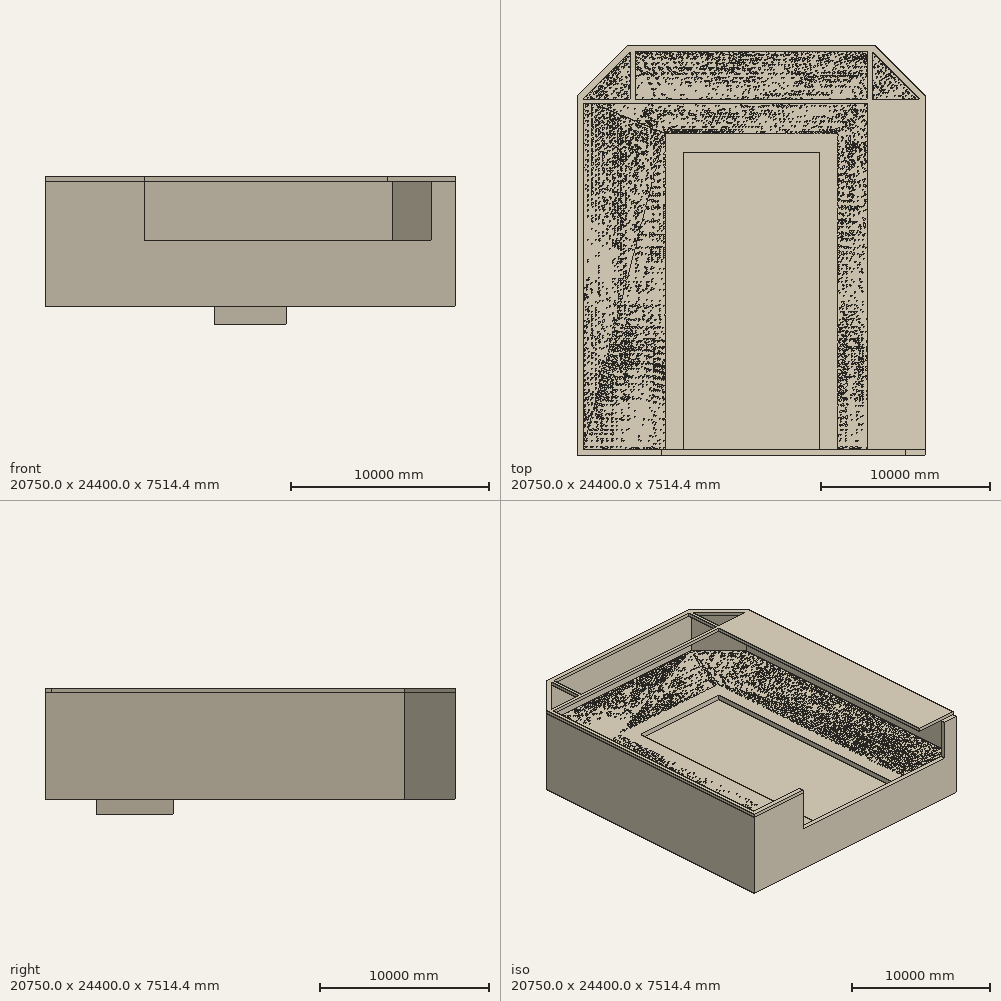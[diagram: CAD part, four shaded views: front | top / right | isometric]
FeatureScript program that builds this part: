
annotation { "Feature Type Name" : "Feature", "Feature Type Description" : "" }
export const myFeature = defineFeature(function(context is Context, id is Id, definition is map)
    precondition{}
    {
        {
            var Q0;
            Q0=qCreatedBy(makeId("Top.planeOp"),FACE);
            var sketch = newSketch(context, id + "F0", { "sketchPlane" : qUnion([Q0])});
            skLineSegment(sketch, "E0.bottom", {"start": v(-7325, 12200) * mm, "end": v(7325, 12200) * mm});
            skLineSegment(sketch, "E0.top", {"start": v(-10375, -12200) * mm, "end": v(10375, -12200) * mm});
            skLineSegment(sketch, "E0.left", {"start": v(-10375, 9150) * mm, "end": v(-10375, -12200) * mm});
            skLineSegment(sketch, "E0.right", {"start": v(10375, 9150) * mm, "end": v(10375, -12200) * mm});
            skLineSegment(sketch, "E1", {"start": v(0, 0) * mm, "end": v(0, -12200) * mm, "construction": true});
            skLineSegment(sketch, "E2", {"start": v(-10375, 0) * mm, "end": v(0, 0) * mm, "construction": true});
            skLineSegment(sketch, "E3", {"start": v(7325, 12200) * mm, "end": v(10375, 9150) * mm});
            skLineSegment(sketch, "E4", {"start": v(-7325, 12200) * mm, "end": v(-10375, 9150) * mm});
            skSolve(sketch);
        }
        {
            var Q0;
            Q0=makeQuery(id+"F0.imprint","IMPRINT",FACE,{"disambiguationData":[TD([[makeQuery(id+"F0.imprint","IMPRINT",EDGE,{"derivedFrom":sQuery(id+"F0.wireOp",EDGE,"E0.bottom")}),-1.0]])]});
            extrude(context, id + "F1", {"entities" : qUnion([Q0]), "offsetDistance" : 25 * mm, "depth" : 6350 * mm});
        }
        {
            var Q0;
            Q0=makeQuery(id+"F1.opExtrude","CAP_FACE",FACE,{"disambiguationData":[OSD([sQuery(id+"F0.wireOp",EDGE,"E0.bottom"),sQuery(id+"F0.wireOp",EDGE,"E0.top"),sQuery(id+"F0.wireOp",EDGE,"E0.left"),sQuery(id+"F0.wireOp",EDGE,"E0.right"),sQuery(id+"F0.wireOp",EDGE,"E3"),sQuery(id+"F0.wireOp",EDGE,"E4")])],"isStart":false});
            shell(context, id + "F2", {"entities" : qUnion([Q0]), "thickness" : 350 * mm});
        }
        {
            var Q0;
            Q0=makeQuery(id+"F1.opExtrude","SWEPT_FACE",FACE,{"disambiguationData":[OSD([sQuery(id+"F0.wireOp",EDGE,"E0.top")])]});
            var sketch = newSketch(context, id + "F3", { "sketchPlane" : qUnion([Q0])});
            skLineSegment(sketch, "E5.bottom", {"start": v(-5375, 6350) * mm, "end": v(9155, 6350) * mm});
            skLineSegment(sketch, "E5.top", {"start": v(-5375, 3350) * mm, "end": v(9155, 3350) * mm});
            skLineSegment(sketch, "E5.left", {"start": v(-5375, 6350) * mm, "end": v(-5375, 3350) * mm});
            skLineSegment(sketch, "E5.right", {"start": v(9155, 6350) * mm, "end": v(9155, 3350) * mm});
            skLineSegment(sketch, "E6.bottom", {"start": v(-4375, 3350) * mm, "end": v(8375, 3350) * mm});
            skLineSegment(sketch, "E6.top", {"start": v(-4375, 310) * mm, "end": v(8375, 310) * mm});
            skLineSegment(sketch, "E6.left", {"start": v(-4375, 3350) * mm, "end": v(-4375, 310) * mm});
            skLineSegment(sketch, "E6.right", {"start": v(8375, 3350) * mm, "end": v(8375, 310) * mm});
            skLineSegment(sketch, "E7.0", {"start": v(-10380, -5) * mm, "end": v(10380, -5) * mm});
            skLineSegment(sketch, "E7.1", {"start": v(-10380, 6355) * mm, "end": v(-10380, -5) * mm});
            skLineSegment(sketch, "E7.2", {"start": v(10380, 6355) * mm, "end": v(-10380, 6355) * mm});
            skLineSegment(sketch, "E7.3", {"start": v(10380, -5) * mm, "end": v(10380, 6355) * mm});
            skSolve(sketch);
        }
        {
            var Q0;
            Q0=makeQuery(id+"F3.imprint","IMPRINT",FACE,{"disambiguationData":[TD([[makeQuery(id+"F3.imprint","IMPRINT",EDGE,{"derivedFrom":sQuery(id+"F3.wireOp",EDGE,"E6.bottom")}),-1.0]])]});
            var Q1;
            Q1=makeQuery(id+"F3.imprint","IMPRINT",FACE,{"disambiguationData":[TD([[makeQuery(id+"F3.imprint","IMPRINT",EDGE,{"derivedFrom":sQuery(id+"F3.wireOp",EDGE,"E5.bottom")}),-1.0]])]});
            var Q2;
            Q2=makeQuery(id+"F2.opShell","OFFSET_FACE",FACE,{"disambiguationData":[OSD([sQuery(id+"F0.wireOp",EDGE,"E0.top")])]});
            extrude(context, id + "F4", {"entities" : qUnion([Q0, Q1]), "operationType" : NewBodyOperationType.REMOVE, "endBound" : BoundingType.UP_TO_SURFACE, "oppositeDirection" : true, "endBoundEntityFace" : qUnion([Q2]), "depth" : 300 * mm, "offsetDistance" : 25 * mm});
        }
        {
            var Q0;
            Q0=makeQuery(id+"F1.opExtrude","CAP_FACE",FACE,{"disambiguationData":[OSD([sQuery(id+"F0.wireOp",EDGE,"E0.bottom"),sQuery(id+"F0.wireOp",EDGE,"E0.top"),sQuery(id+"F0.wireOp",EDGE,"E0.left"),sQuery(id+"F0.wireOp",EDGE,"E0.right"),sQuery(id+"F0.wireOp",EDGE,"E3"),sQuery(id+"F0.wireOp",EDGE,"E4")])],"isStart":false});
            var sketch = newSketch(context, id + "F5", { "sketchPlane" : qUnion([Q0])});
            skLineSegment(sketch, "E8.0", {"start": v(-10375, 9150) * mm, "end": v(-10375, -12200) * mm});
            skLineSegment(sketch, "E8.1", {"start": v(-7325, 12200) * mm, "end": v(-10375, 9150) * mm});
            skLineSegment(sketch, "E8.2", {"start": v(-7325, 12200) * mm, "end": v(7325, 12200) * mm});
            skLineSegment(sketch, "E8.3", {"start": v(7325, 12200) * mm, "end": v(10375, 9150) * mm});
            skLineSegment(sketch, "E8.4", {"start": v(10375, 9150) * mm, "end": v(10375, -12200) * mm});
            skLineSegment(sketch, "E8.5", {"start": v(-10375, -12200) * mm, "end": v(-5375, -12200) * mm});
            skLineSegment(sketch, "E8.6", {"start": v(-10025, 9005.03) * mm, "end": v(-10025, -11850) * mm});
            skLineSegment(sketch, "E8.7", {"start": v(-7180.03, 11850) * mm, "end": v(-10025, 9005.03) * mm});
            skLineSegment(sketch, "E8.8", {"start": v(-7180.03, 11850) * mm, "end": v(7180.03, 11850) * mm});
            skLineSegment(sketch, "E8.9", {"start": v(7180.03, 11850) * mm, "end": v(10025, 9005.03) * mm});
            skLineSegment(sketch, "E8.10", {"start": v(10025, 9005.03) * mm, "end": v(10025, -11850) * mm});
            skLineSegment(sketch, "E8.11", {"start": v(-10025, -11850) * mm, "end": v(-5000, -11850) * mm});
            skLineSegment(sketch, "E9.bottom", {"start": v(-5000, -11850) * mm, "end": v(10375, -11850) * mm});
            skLineSegment(sketch, "E9.top", {"start": v(-5000, -12200) * mm, "end": v(10375, -12200) * mm});
            skLineSegment(sketch, "E9.right", {"start": v(10375, -11850) * mm, "end": v(10375, -12200) * mm});
            skLineSegment(sketch, "E10", {"start": v(-10025, 9005.03) * mm, "end": v(-7180.03, 9005.03) * mm});
            skLineSegment(sketch, "E11", {"start": v(-7180.03, 9005.03) * mm, "end": v(-7180.03, 11850) * mm});
            skLineSegment(sketch, "E12", {"start": v(7180.03, 11850) * mm, "end": v(7180.03, 9005.03) * mm});
            skLineSegment(sketch, "E13", {"start": v(7180.03, 9005.03) * mm, "end": v(10025, 9005.03) * mm});
            skLineSegment(sketch, "E14", {"start": v(-7180.03, 9005.03) * mm, "end": v(7180.03, 9005.03) * mm});
            skLineSegment(sketch, "E15", {"start": v(-7180.03, 9005.03) * mm, "end": v(-7180.03, -7244.51) * mm});
            skLineSegment(sketch, "E16", {"start": v(7180.03, 9005.03) * mm, "end": v(7180.03, -11850) * mm});
            skLineSegment(sketch, "E17", {"start": v(-10025, 8751.03) * mm, "end": v(10025, 8751.03) * mm});
            skLineSegment(sketch, "E18", {"start": v(-6926.03, 11850) * mm, "end": v(-6926.03, -11850) * mm});
            skLineSegment(sketch, "E19", {"start": v(6926.03, 11850) * mm, "end": v(6926.03, -11850) * mm});
            skSolve(sketch);
        }
        {
            var Q0;
            Q0=makeQuery(id+"F5.imprint","IMPRINT",FACE,{"disambiguationData":[TD([[makeQuery(id+"F5.imprint","IMPRINT",EDGE,{"derivedFrom":sQuery(id+"F5.wireOp",EDGE,"E8.0")}),1.0]])]});
            var Q1;
            {var subQ0=sQuery(id+"F5.wireOp",EDGE,"E9.left");Q1=makeQuery(id+"F5.imprint","IMPRINT",FACE,{"disambiguationData":[TD([[makeQuery(id+"F5.imprint","IMPRINT",EDGE,{"derivedFrom":subQ0}),1.0]])]});}
            var Q2;
            {var subQ0=sQuery(id+"F5.wireOp",EDGE,"E9.right");Q2=makeQuery(id+"F5.imprint","IMPRINT",FACE,{"disambiguationData":[TD([[makeQuery(id+"F5.imprint","IMPRINT",EDGE,{"derivedFrom":subQ0}),-1.0]])]});}
            var Q3;
            {var subQ0=sQuery(id+"F5.wireOp",EDGE,"E10");Q3=makeQuery(id+"F5.imprint","IMPRINT",FACE,{"disambiguationData":[TD([[makeQuery(id+"F5.imprint","IMPRINT",EDGE,{"derivedFrom":subQ0}),-1.0]])]});}
            var Q4;
            {var subQ0=sQuery(id+"F5.wireOp",EDGE,"E15");var subQ5=sQuery(id+"F5.wireOp",EDGE,"E17");var subQ6=makeQuery(id+"F5.imprint","INTERSECT",VERTEX,{"derivedFrom":[subQ0,subQ5]});Q4=makeQuery(id+"F5.imprint","IMPRINT",FACE,{"disambiguationData":[TD([[makeQuery(id+"F5.imprint","IMPRINT",EDGE,{"disambiguationData":[TD([[subQ6,-1.0]])],"derivedFrom":subQ5}),1.0]])]});}
            var Q5;
            {var subQ0=sQuery(id+"F5.wireOp",EDGE,"E11");Q5=makeQuery(id+"F5.imprint","IMPRINT",FACE,{"disambiguationData":[TD([[makeQuery(id+"F5.imprint","IMPRINT",EDGE,{"derivedFrom":subQ0}),-1.0]])]});}
            var Q6;
            {var subQ0=sQuery(id+"F5.wireOp",EDGE,"E18");var subQ1=sQuery(id+"F5.wireOp",EDGE,"E14");var subQ2=makeQuery(id+"F5.imprint","INTERSECT",VERTEX,{"derivedFrom":[subQ1,subQ0]});Q6=makeQuery(id+"F5.imprint","IMPRINT",FACE,{"disambiguationData":[TD([[makeQuery(id+"F5.imprint","IMPRINT",EDGE,{"disambiguationData":[TD([[subQ2,-1.0]])],"derivedFrom":subQ1}),-1.0]])]});}
            var Q7;
            {var subQ0=sQuery(id+"F5.wireOp",EDGE,"E12");Q7=makeQuery(id+"F5.imprint","IMPRINT",FACE,{"disambiguationData":[TD([[makeQuery(id+"F5.imprint","IMPRINT",EDGE,{"derivedFrom":subQ0}),-1.0]])]});}
            var Q8;
            {var subQ0=sQuery(id+"F5.wireOp",EDGE,"E16");var subQ5=sQuery(id+"F5.wireOp",EDGE,"E17");var subQ6=makeQuery(id+"F5.imprint","INTERSECT",VERTEX,{"derivedFrom":[subQ0,subQ5]});Q8=makeQuery(id+"F5.imprint","IMPRINT",FACE,{"disambiguationData":[TD([[makeQuery(id+"F5.imprint","IMPRINT",EDGE,{"disambiguationData":[TD([[subQ6,1.0]])],"derivedFrom":subQ5}),1.0]])]});}
            var Q9;
            {var subQ0=sQuery(id+"F5.wireOp",EDGE,"E13");Q9=makeQuery(id+"F5.imprint","IMPRINT",FACE,{"disambiguationData":[TD([[makeQuery(id+"F5.imprint","IMPRINT",EDGE,{"derivedFrom":subQ0}),-1.0]])]});}
            var Q10;
            {var subQ0=sQuery(id+"F5.wireOp",EDGE,"E16");var subQ1=sQuery(id+"F5.wireOp",EDGE,"E9.bottom");var subQ2=makeQuery(id+"F5.imprint","INTERSECT",VERTEX,{"derivedFrom":[subQ1,subQ0]});Q10=makeQuery(id+"F5.imprint","IMPRINT",FACE,{"disambiguationData":[TD([[makeQuery(id+"F5.imprint","IMPRINT",EDGE,{"disambiguationData":[TD([[subQ2,1.0]])],"derivedFrom":subQ1}),1.0]])]});}
            var Q11;
            {var subQ0=sQuery(id+"F5.wireOp",EDGE,"E18");var subQ1=sQuery(id+"F5.wireOp",EDGE,"E9.bottom");var subQ2=makeQuery(id+"F5.imprint","INTERSECT",VERTEX,{"derivedFrom":[subQ1,subQ0]});Q11=makeQuery(id+"F5.imprint","IMPRINT",FACE,{"disambiguationData":[TD([[makeQuery(id+"F5.imprint","IMPRINT",EDGE,{"disambiguationData":[TD([[subQ2,1.0]])],"derivedFrom":subQ1}),1.0]])]});}
            var Q12;
            {var subQ3=sQuery(id+"F3.wireOp",EDGE,"E5.bottom");var subQ4=sQuery(id+"F0.wireOp",EDGE,"E0.top");var subQ5=makeQuery(id+"F4.boolean.opBoolean","COPY",EDGE,{"derivedFrom":makeQuery(id+"F4.opExtrude","SWEPT_EDGE",EDGE,{"disambiguationData":[OSD([subQ4,subQ3,sQuery(id+"F3.wireOp",EDGE,"E5.left")])]})});Q12=makeQuery(id+"F5.imprint","IMPRINT",FACE,{"disambiguationData":[TD([[makeQuery(id+"F5.imprint","IMPRINT",EDGE,{"derivedFrom":subQ5}),1.0]])]});}
            extrude(context, id + "F6", {"entities" : qUnion([Q0, Q1, Q2, Q3, Q4, Q5, Q6, Q7, Q8, Q9, Q10, Q11, Q12]), "depth" : 250 * mm});
        }
        {
            var Q0;
            Q0=makeQuery(id+"F1.opExtrude","CAP_FACE",FACE,{"disambiguationData":[OSD([sQuery(id+"F0.wireOp",EDGE,"E0.bottom"),sQuery(id+"F0.wireOp",EDGE,"E0.top"),sQuery(id+"F0.wireOp",EDGE,"E0.left"),sQuery(id+"F0.wireOp",EDGE,"E0.right"),sQuery(id+"F0.wireOp",EDGE,"E3"),sQuery(id+"F0.wireOp",EDGE,"E4")])],"isStart":true});
            var sketch = newSketch(context, id + "F7", { "sketchPlane" : qUnion([Q0])});
            skLineSegment(sketch, "E20.bottom", {"start": v(-1828.8, 9152) * mm, "end": v(1828.8, 9152) * mm});
            skLineSegment(sketch, "E20.top", {"start": v(-1828.8, 4580) * mm, "end": v(1828.8, 4580) * mm});
            skLineSegment(sketch, "E20.left", {"start": v(-1828.8, 9152) * mm, "end": v(-1828.8, 4580) * mm});
            skLineSegment(sketch, "E20.right", {"start": v(1828.8, 9152) * mm, "end": v(1828.8, 4580) * mm});
            skLineSegment(sketch, "E21", {"start": v(0, 9152) * mm, "end": v(0, 12200) * mm, "construction": true});
            skSolve(sketch);
        }
        {
            var Q0;
            Q0=makeQuery(id+"F7.imprint","IMPRINT",FACE,{"disambiguationData":[TD([[makeQuery(id+"F7.imprint","IMPRINT",EDGE,{"derivedFrom":sQuery(id+"F7.wireOp",EDGE,"E20.bottom")}),-1.0]])]});
            extrude(context, id + "F8", {"entities" : qUnion([Q0]), "operationType" : NewBodyOperationType.ADD, "depth" : 914.4 * mm, "offsetDistance" : 25 * mm});
        }
        {
            var Q0;
            {var subQ0=sQuery(id+"F3.wireOp",EDGE,"E5.top");Q0=makeQuery(id+"F4.boolean.opBoolean","COPY",FACE,{"derivedFrom":makeQuery(id+"F4.opExtrude","SWEPT_FACE",FACE,{"disambiguationData":[OSD([subQ0]),TDD([makeQuery(id+"F3.imprint","IMPRINT",EDGE,{"disambiguationData":[TD([[makeQuery(id+"F3.imprint","INTERSECT",VERTEX,{"derivedFrom":[subQ0,sQuery(id+"F3.wireOp",EDGE,"E5.left")]}),-1.0]])],"derivedFrom":subQ0})])]})});}
            var sketch = newSketch(context, id + "F9", { "sketchPlane" : qUnion([Q0])});
            skLineSegment(sketch, "E22", {"start": v(-10025, -11850) * mm, "end": v(-10025, 9005.03) * mm});
            skLineSegment(sketch, "E23", {"start": v(-10025, 9005.03) * mm, "end": v(-7180.03, 11850) * mm});
            skLineSegment(sketch, "E24", {"start": v(-7180.03, 11850) * mm, "end": v(7180.03, 11850) * mm});
            skLineSegment(sketch, "E25", {"start": v(7180.03, 11850) * mm, "end": v(10025, 9005.03) * mm});
            skLineSegment(sketch, "E26", {"start": v(10025, 9005.03) * mm, "end": v(10025, -11850) * mm});
            skLineSegment(sketch, "E27", {"start": v(10025, -11850) * mm, "end": v(5148.2, -11850) * mm});
            skLineSegment(sketch, "E28", {"start": v(5148.2, -11850) * mm, "end": v(5148.2, 6973.2) * mm});
            skLineSegment(sketch, "E29", {"start": v(5148.2, 6973.2) * mm, "end": v(-5148.2, 6973.2) * mm});
            skLineSegment(sketch, "E30", {"start": v(-5148.2, 6973.2) * mm, "end": v(-5148.2, -11850) * mm});
            skLineSegment(sketch, "E31", {"start": v(-5148.2, -11850) * mm, "end": v(-10025, -11850) * mm});
            skSolve(sketch);
        }
        {
            var Q0;
            {var subQ5=sQuery(id+"F9.wireOp",EDGE,"E22");Q0=makeQuery(id+"F9.imprint","IMPRINT",FACE,{"disambiguationData":[TD([[makeQuery(id+"F9.imprint","IMPRINT",EDGE,{"derivedFrom":subQ5}),-1.0]])]});}
            extrude(context, id + "F10", {"entities" : qUnion([Q0]), "oppositeDirection" : true, "depth" : 300 * mm, "offsetDistance" : 25 * mm});
        }
        {
            var Q0;
            {var subQ0=sQuery(id+"F3.wireOp",EDGE,"E5.top");Q0=makeQuery(id+"F4.boolean.opBoolean","COPY",FACE,{"derivedFrom":makeQuery(id+"F4.opExtrude","SWEPT_FACE",FACE,{"disambiguationData":[OSD([subQ0]),TDD([makeQuery(id+"F3.imprint","IMPRINT",EDGE,{"disambiguationData":[TD([[makeQuery(id+"F3.imprint","INTERSECT",VERTEX,{"derivedFrom":[subQ0,sQuery(id+"F3.wireOp",EDGE,"E5.left")]}),-1.0]])],"derivedFrom":subQ0})])]})});}
            var sketch = newSketch(context, id + "F11", { "sketchPlane" : qUnion([Q0])});
            skLineSegment(sketch, "E32", {"start": v(-10025, -11850) * mm, "end": v(-4025, -11850) * mm});
            skLineSegment(sketch, "E33", {"start": v(-4025, -11850) * mm, "end": v(-4025, 5850) * mm});
            skLineSegment(sketch, "E34", {"start": v(-4025, 5850) * mm, "end": v(4025, 5850) * mm});
            skLineSegment(sketch, "E35", {"start": v(4025, 5850) * mm, "end": v(4025, -11850) * mm});
            skLineSegment(sketch, "E36", {"start": v(4025, -11850) * mm, "end": v(10025, -11850) * mm});
            skLineSegment(sketch, "E37", {"start": v(10025, -11850) * mm, "end": v(10025, 9005.03) * mm});
            skLineSegment(sketch, "E38", {"start": v(10025, 9005.03) * mm, "end": v(7180.03, 11850) * mm});
            skLineSegment(sketch, "E39", {"start": v(7180.03, 11850) * mm, "end": v(-7180.03, 11850) * mm});
            skLineSegment(sketch, "E40", {"start": v(-7180.03, 11850) * mm, "end": v(-10025, 9005.03) * mm});
            skLineSegment(sketch, "E41", {"start": v(-10025, 9005.03) * mm, "end": v(-10025, -11850) * mm});
            skSolve(sketch);
        }
        {
            var Q0;
            Q0 = qSketchRegion(id + "F11", true);
            extrude(context, id + "F12", {"entities" : qUnion([Q0]), "oppositeDirection" : true, "depth" : 350 * mm, "offsetDistance" : 25 * mm});
        }
    });
